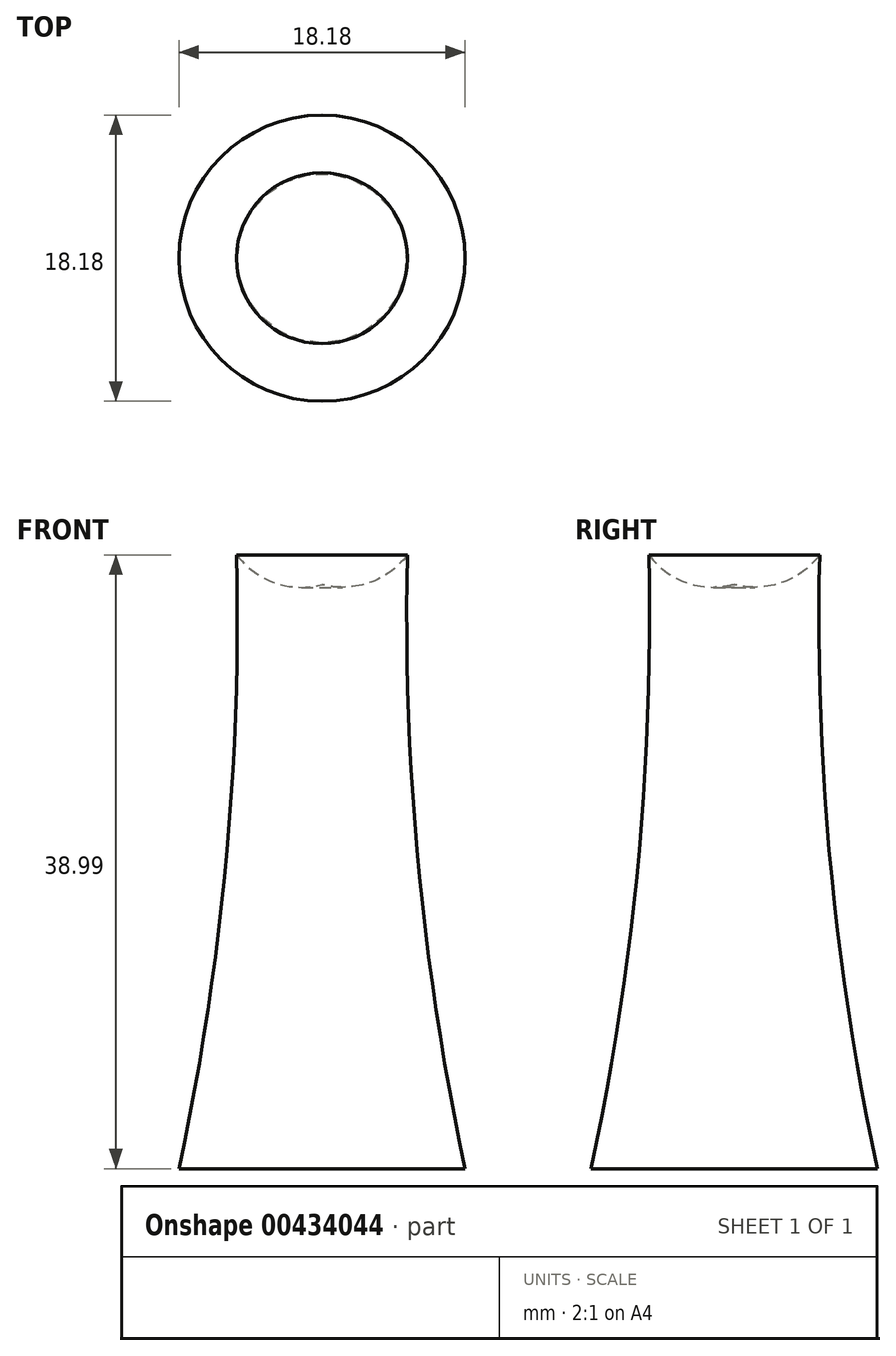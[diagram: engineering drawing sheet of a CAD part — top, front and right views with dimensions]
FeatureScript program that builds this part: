
annotation { "Feature Type Name" : "Feature", "Feature Type Description" : "" }
export const myFeature = defineFeature(function(context is Context, id is Id, definition is map)
    precondition{}
    {
        {
            var Q0;
            Q0=qCreatedBy(makeId("Front.planeOp"),FACE);
            var sketch = newSketch(context, id + "F0", { "sketchPlane" : qUnion([Q0])});
            skArc(sketch, "E0", {"start": v(0, 47.04) * mm, "mid": v(-5.57, 44.94) * mm, "end": v(-5.43, 39) * mm});
            skArc(sketch, "E1", {"start": v(-9.09, 0) * mm, "mid": v(-6.11, 19.39) * mm, "end": v(-5.43, 39) * mm});
            skLineSegment(sketch, "E2", {"start": v(-9.09, 0) * mm, "end": v(0, 0) * mm});
            skLineSegment(sketch, "E3", {"start": v(0, 0) * mm, "end": v(0, 47.04) * mm});
            skSolve(sketch);
        }
        {
            var Q0;
            Q0=makeQuery(id+"F0.imprint","IMPRINT",FACE,{"disambiguationData":[TD([[makeQuery(id+"F0.imprint","IMPRINT",EDGE,{"derivedFrom":sQuery(id+"F0.wireOp",EDGE,"E0")}),1.0]])]});
            var Q1;
            Q1=sQuery(id+"F0.wireOp",EDGE,"E3");
            revolve(context, id + "F1", {"entities" : qUnion([Q0]), "axis" : qUnion([Q1]), "revolveType" : RevolveType.FULL});
        }
    });
